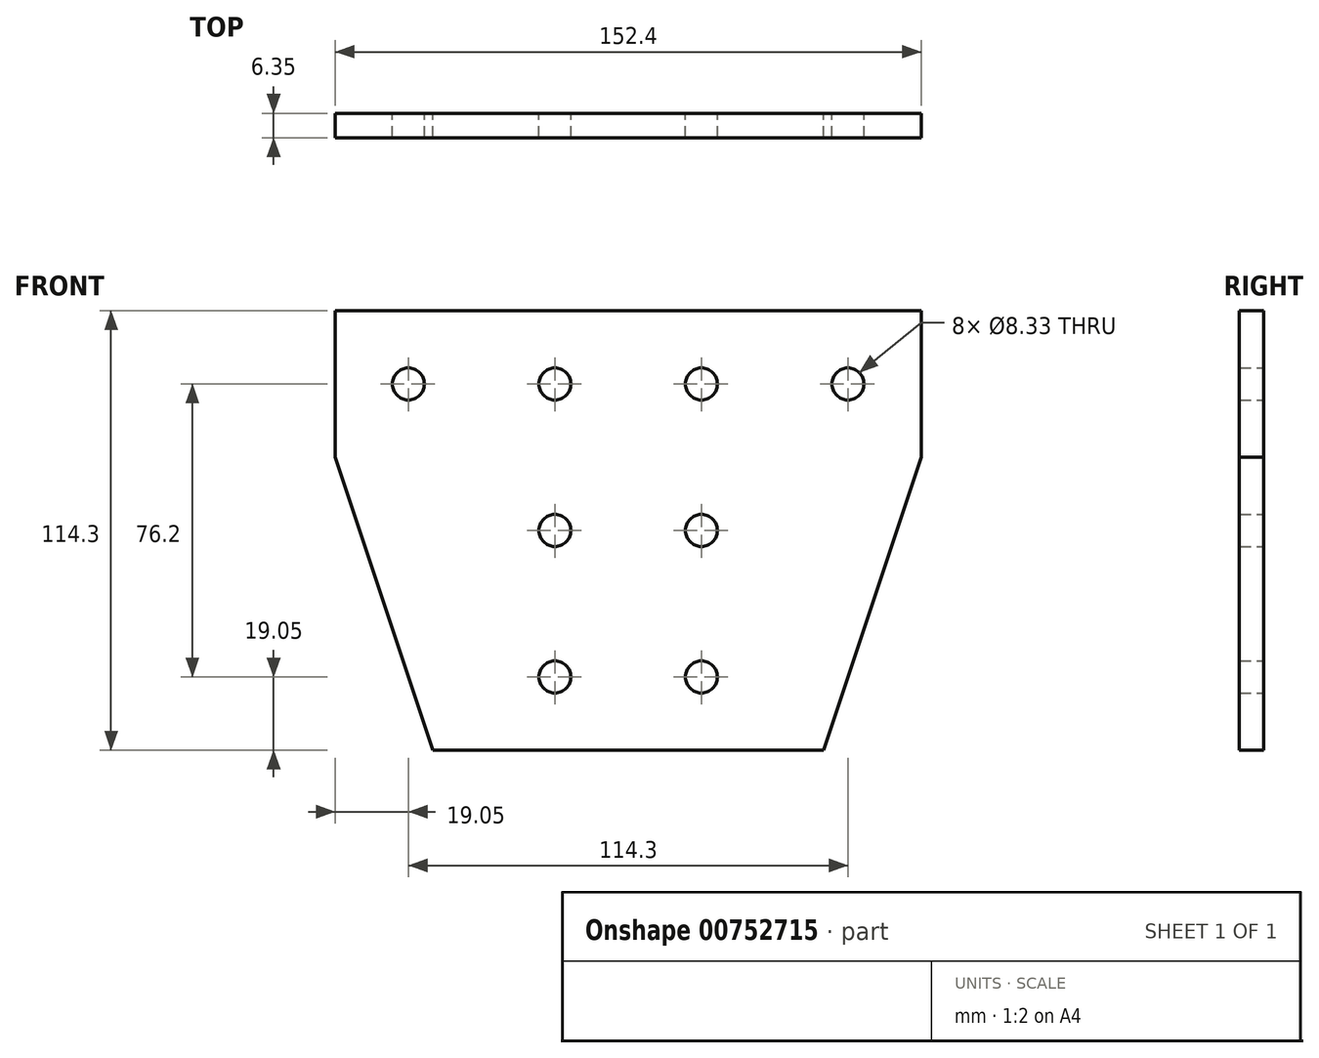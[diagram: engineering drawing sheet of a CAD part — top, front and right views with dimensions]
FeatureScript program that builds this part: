
annotation { "Feature Type Name" : "Feature", "Feature Type Description" : "" }
export const myFeature = defineFeature(function(context is Context, id is Id, definition is map)
    precondition{}
    {
        {
            var Q0;
            Q0=qCreatedBy(makeId("Front.planeOp"),FACE);
            var sketch = newSketch(context, id + "F0", { "sketchPlane" : qUnion([Q0])});
            skLineSegment(sketch, "E0", {"start": v(-76.2, 57.15) * mm, "end": v(76.2, 57.15) * mm});
            skLineSegment(sketch, "E1", {"start": v(76.2, 57.15) * mm, "end": v(76.2, 19.05) * mm});
            skLineSegment(sketch, "E2", {"start": v(-76.2, 57.15) * mm, "end": v(-76.2, 19.05) * mm});
            skLineSegment(sketch, "E3", {"start": v(-50.8, -57.15) * mm, "end": v(50.8, -57.15) * mm});
            skLineSegment(sketch, "E4", {"start": v(-76.2, 19.05) * mm, "end": v(-50.8, -57.15) * mm});
            skLineSegment(sketch, "E5", {"start": v(50.8, -57.15) * mm, "end": v(76.2, 19.05) * mm});
            skPoint(sketch, "E6", {"position": v(-57.15, 38.1) * mm});
            skPoint(sketch, "E7", {"position": v(-19.05, 38.1) * mm});
            skPoint(sketch, "E8", {"position": v(19.05, 38.1) * mm});
            skPoint(sketch, "E9", {"position": v(57.15, 38.1) * mm});
            skPoint(sketch, "E10", {"position": v(-19.05, 0) * mm});
            skPoint(sketch, "E11", {"position": v(-19.05, -38.1) * mm});
            skPoint(sketch, "E12", {"position": v(19.05, 0) * mm});
            skPoint(sketch, "E13", {"position": v(19.05, -38.1) * mm});
            skSolve(sketch);
        }
        {
            var Q0;
            Q0=makeQuery(id+"F0.imprint","IMPRINT",FACE,{"disambiguationData":[TD([[makeQuery(id+"F0.imprint","IMPRINT",EDGE,{"derivedFrom":sQuery(id+"F0.wireOp",EDGE,"E0")}),-1.0]])]});
            extrude(context, id + "F1", {"entities" : qUnion([Q0]), "depth" : 6.35 * mm, "offsetDistance" : 25.4 * mm});
        }
        {
            var Q0;
            Q0=sQuery(id+"F0.wireOp",VERTEX,"E9");
            var Q1;
            Q1=makeQuery(id+"F1.opExtrude","SWEPT_BODY",BODY,{"disambiguationData":[OSD([sQuery(id+"F0.wireOp",EDGE,"E0"),sQuery(id+"F0.wireOp",EDGE,"E1"),sQuery(id+"F0.wireOp",EDGE,"E2"),sQuery(id+"F0.wireOp",EDGE,"E3"),sQuery(id+"F0.wireOp",EDGE,"E4"),sQuery(id+"F0.wireOp",EDGE,"E5")])]});
            hole(context, id + "F2", {"style" : HoleStyle.SIMPLE, "endStyle" : HoleEndStyle.THROUGH, "oppositeDirection" : true, "holeDiameter" : 8.33 * mm, "majorDiameter" : 6.35 * mm, "isTappedThrough" : true, "tappedDepth" : 25.4 * mm, "tapClearance" : 3, "startFromSketch" : true, "locations" : qUnion([Q0]), "scope" : qUnion([Q1])});
        }
        {
            var Q0;
            Q0=sQuery(id+"F0.wireOp",VERTEX,"E8");
            var Q1;
            Q1=makeQuery(id+"F1.opExtrude","SWEPT_BODY",BODY,{"disambiguationData":[OSD([sQuery(id+"F0.wireOp",EDGE,"E0"),sQuery(id+"F0.wireOp",EDGE,"E1"),sQuery(id+"F0.wireOp",EDGE,"E2"),sQuery(id+"F0.wireOp",EDGE,"E3"),sQuery(id+"F0.wireOp",EDGE,"E4"),sQuery(id+"F0.wireOp",EDGE,"E5")])]});
            hole(context, id + "F3", {"style" : HoleStyle.SIMPLE, "endStyle" : HoleEndStyle.THROUGH, "oppositeDirection" : true, "holeDiameter" : 8.33 * mm, "majorDiameter" : 6.35 * mm, "isTappedThrough" : true, "tappedDepth" : 25.4 * mm, "tapClearance" : 3, "startFromSketch" : true, "locations" : qUnion([Q0]), "scope" : qUnion([Q1])});
        }
        {
            var Q0;
            Q0=sQuery(id+"F0.wireOp",VERTEX,"E7");
            var Q1;
            Q1=makeQuery(id+"F1.opExtrude","SWEPT_BODY",BODY,{"disambiguationData":[OSD([sQuery(id+"F0.wireOp",EDGE,"E0"),sQuery(id+"F0.wireOp",EDGE,"E1"),sQuery(id+"F0.wireOp",EDGE,"E2"),sQuery(id+"F0.wireOp",EDGE,"E3"),sQuery(id+"F0.wireOp",EDGE,"E4"),sQuery(id+"F0.wireOp",EDGE,"E5")])]});
            hole(context, id + "F4", {"style" : HoleStyle.SIMPLE, "endStyle" : HoleEndStyle.THROUGH, "oppositeDirection" : true, "holeDiameter" : 8.33 * mm, "majorDiameter" : 6.35 * mm, "isTappedThrough" : true, "tappedDepth" : 25.4 * mm, "tapClearance" : 3, "startFromSketch" : true, "locations" : qUnion([Q0]), "scope" : qUnion([Q1])});
        }
        {
            var Q0;
            Q0=sQuery(id+"F0.wireOp",VERTEX,"E6");
            var Q1;
            Q1=makeQuery(id+"F1.opExtrude","SWEPT_BODY",BODY,{"disambiguationData":[OSD([sQuery(id+"F0.wireOp",EDGE,"E0"),sQuery(id+"F0.wireOp",EDGE,"E1"),sQuery(id+"F0.wireOp",EDGE,"E2"),sQuery(id+"F0.wireOp",EDGE,"E3"),sQuery(id+"F0.wireOp",EDGE,"E4"),sQuery(id+"F0.wireOp",EDGE,"E5")])]});
            hole(context, id + "F5", {"style" : HoleStyle.SIMPLE, "endStyle" : HoleEndStyle.THROUGH, "oppositeDirection" : true, "holeDiameter" : 8.33 * mm, "majorDiameter" : 6.35 * mm, "isTappedThrough" : true, "tappedDepth" : 25.4 * mm, "tapClearance" : 3, "startFromSketch" : true, "locations" : qUnion([Q0]), "scope" : qUnion([Q1])});
        }
        {
            var Q0;
            Q0=sQuery(id+"F0.wireOp",VERTEX,"E10");
            var Q1;
            Q1=makeQuery(id+"F1.opExtrude","SWEPT_BODY",BODY,{"disambiguationData":[OSD([sQuery(id+"F0.wireOp",EDGE,"E0"),sQuery(id+"F0.wireOp",EDGE,"E1"),sQuery(id+"F0.wireOp",EDGE,"E2"),sQuery(id+"F0.wireOp",EDGE,"E3"),sQuery(id+"F0.wireOp",EDGE,"E4"),sQuery(id+"F0.wireOp",EDGE,"E5")])]});
            hole(context, id + "F6", {"style" : HoleStyle.SIMPLE, "endStyle" : HoleEndStyle.THROUGH, "oppositeDirection" : true, "holeDiameter" : 8.33 * mm, "majorDiameter" : 6.35 * mm, "isTappedThrough" : true, "tappedDepth" : 25.4 * mm, "tapClearance" : 3, "startFromSketch" : true, "locations" : qUnion([Q0]), "scope" : qUnion([Q1])});
        }
        {
            var Q0;
            Q0=sQuery(id+"F0.wireOp",VERTEX,"E12");
            var Q1;
            Q1=makeQuery(id+"F1.opExtrude","SWEPT_BODY",BODY,{"disambiguationData":[OSD([sQuery(id+"F0.wireOp",EDGE,"E0"),sQuery(id+"F0.wireOp",EDGE,"E1"),sQuery(id+"F0.wireOp",EDGE,"E2"),sQuery(id+"F0.wireOp",EDGE,"E3"),sQuery(id+"F0.wireOp",EDGE,"E4"),sQuery(id+"F0.wireOp",EDGE,"E5")])]});
            hole(context, id + "F7", {"style" : HoleStyle.SIMPLE, "endStyle" : HoleEndStyle.THROUGH, "oppositeDirection" : true, "holeDiameter" : 8.33 * mm, "majorDiameter" : 6.35 * mm, "isTappedThrough" : true, "tappedDepth" : 25.4 * mm, "tapClearance" : 3, "startFromSketch" : true, "locations" : qUnion([Q0]), "scope" : qUnion([Q1])});
        }
        {
            var Q0;
            Q0=sQuery(id+"F0.wireOp",VERTEX,"E11");
            var Q1;
            Q1=makeQuery(id+"F1.opExtrude","SWEPT_BODY",BODY,{"disambiguationData":[OSD([sQuery(id+"F0.wireOp",EDGE,"E0"),sQuery(id+"F0.wireOp",EDGE,"E1"),sQuery(id+"F0.wireOp",EDGE,"E2"),sQuery(id+"F0.wireOp",EDGE,"E3"),sQuery(id+"F0.wireOp",EDGE,"E4"),sQuery(id+"F0.wireOp",EDGE,"E5")])]});
            hole(context, id + "F8", {"style" : HoleStyle.SIMPLE, "endStyle" : HoleEndStyle.THROUGH, "oppositeDirection" : true, "holeDiameter" : 8.33 * mm, "majorDiameter" : 6.35 * mm, "isTappedThrough" : true, "tappedDepth" : 25.4 * mm, "tapClearance" : 3, "startFromSketch" : true, "locations" : qUnion([Q0]), "scope" : qUnion([Q1])});
        }
        {
            var Q0;
            Q0=sQuery(id+"F0.wireOp",VERTEX,"E13");
            var Q1;
            Q1=makeQuery(id+"F1.opExtrude","SWEPT_BODY",BODY,{"disambiguationData":[OSD([sQuery(id+"F0.wireOp",EDGE,"E0"),sQuery(id+"F0.wireOp",EDGE,"E1"),sQuery(id+"F0.wireOp",EDGE,"E2"),sQuery(id+"F0.wireOp",EDGE,"E3"),sQuery(id+"F0.wireOp",EDGE,"E4"),sQuery(id+"F0.wireOp",EDGE,"E5")])]});
            hole(context, id + "F9", {"style" : HoleStyle.SIMPLE, "endStyle" : HoleEndStyle.THROUGH, "oppositeDirection" : true, "holeDiameter" : 8.33 * mm, "majorDiameter" : 6.35 * mm, "isTappedThrough" : true, "tappedDepth" : 25.4 * mm, "tapClearance" : 3, "startFromSketch" : true, "locations" : qUnion([Q0]), "scope" : qUnion([Q1])});
        }
    });
